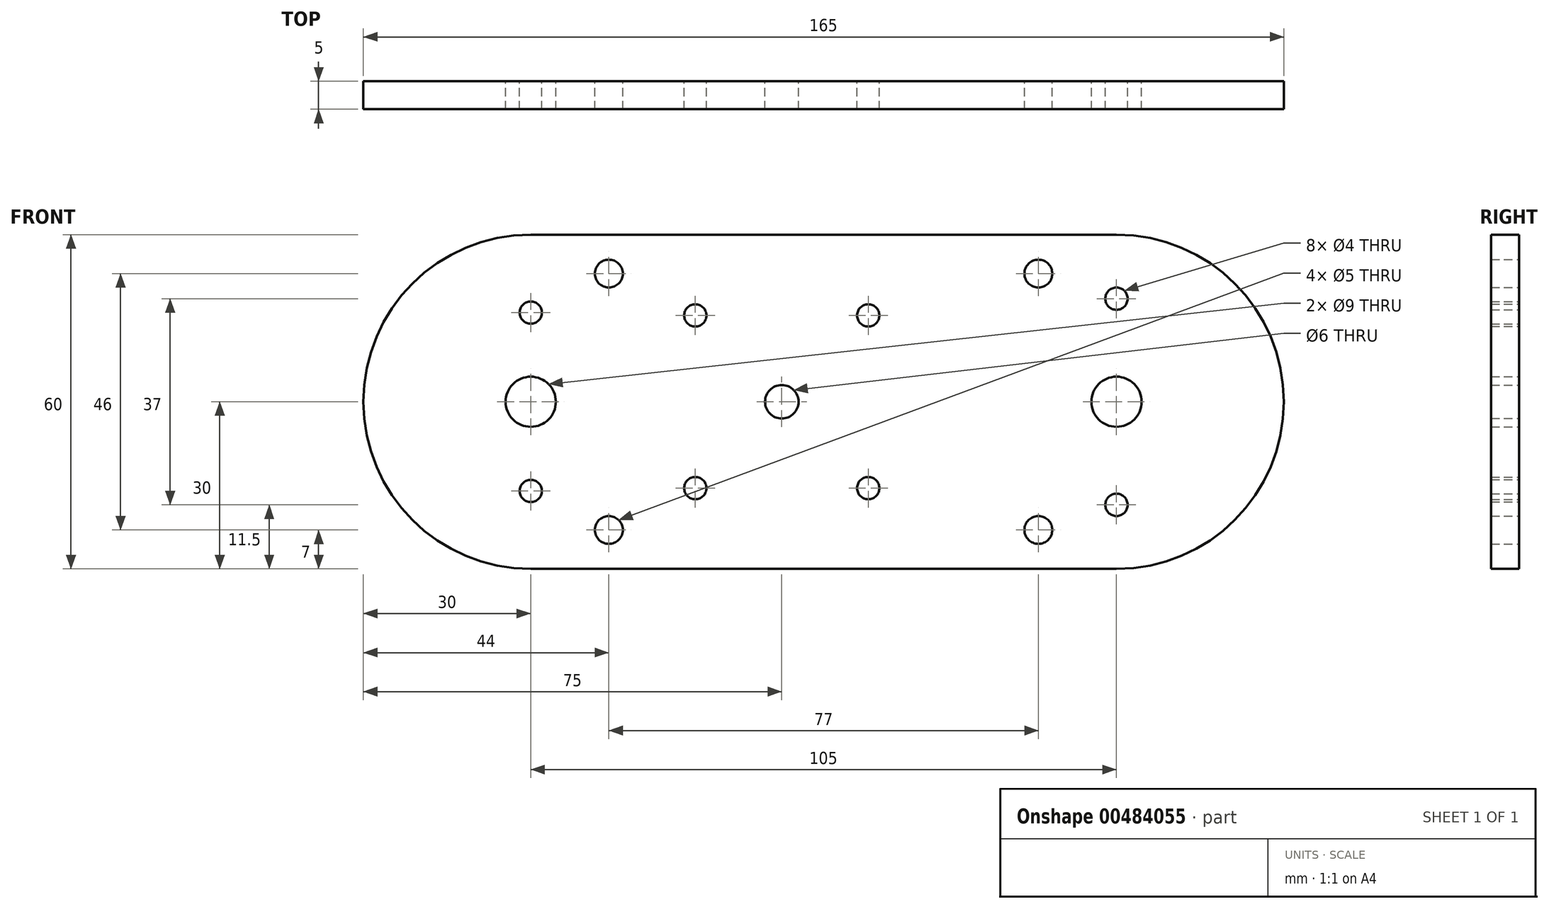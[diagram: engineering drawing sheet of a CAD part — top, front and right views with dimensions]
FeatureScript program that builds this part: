
annotation { "Feature Type Name" : "Feature", "Feature Type Description" : "" }
export const myFeature = defineFeature(function(context is Context, id is Id, definition is map)
    precondition{}
    {
        {
            var Q0;
            Q0=qCreatedBy(makeId("Front.planeOp"),FACE);
            var sketch = newSketch(context, id + "F0", { "sketchPlane" : qUnion([Q0])});
            skLineSegment(sketch, "E0.bottom", {"start": v(52.5, 30) * mm, "end": v(-52.5, 30) * mm});
            skLineSegment(sketch, "E0.top", {"start": v(52.5, -30) * mm, "end": v(-52.5, -30) * mm});
            skPoint(sketch, "E0.middle", {"position": v(0, 0) * mm});
            skArc(sketch, "E1", {"start": v(-52.5, 30) * mm, "mid": v(-82.5, 0) * mm, "end": v(-52.5, -30) * mm});
            skArc(sketch, "E2", {"start": v(52.5, 30) * mm, "mid": v(82.5, 0) * mm, "end": v(52.5, -30) * mm});
            skCircle(sketch, "E3", {"center": v(-52.5, 0) * mm, "radius": 4.5 * mm});
            skCircle(sketch, "E4", {"center": v(52.5, 0) * mm, "radius": 4.5 * mm});
            skPoint(sketch, "E5.middle", {"position": v(-7.5, 0) * mm});
            skCircle(sketch, "E6", {"center": v(-23, 15.5) * mm, "radius": 2 * mm});
            skCircle(sketch, "E7", {"center": v(8, 15.5) * mm, "radius": 2 * mm});
            skCircle(sketch, "E8", {"center": v(8, -15.5) * mm, "radius": 2 * mm});
            skCircle(sketch, "E9", {"center": v(-23, -15.5) * mm, "radius": 2 * mm});
            skCircle(sketch, "E10", {"center": v(-52.5, 16) * mm, "radius": 2 * mm});
            skCircle(sketch, "E11", {"center": v(-52.5, -16) * mm, "radius": 2 * mm});
            skCircle(sketch, "E12", {"center": v(52.5, 18.5) * mm, "radius": 2 * mm});
            skCircle(sketch, "E13", {"center": v(52.5, -18.5) * mm, "radius": 2 * mm});
            skCircle(sketch, "E14", {"center": v(-38.5, 23) * mm, "radius": 2.5 * mm});
            skCircle(sketch, "E15", {"center": v(-38.5, -23) * mm, "radius": 2.5 * mm});
            skCircle(sketch, "E16", {"center": v(38.5, -23) * mm, "radius": 2.5 * mm});
            skCircle(sketch, "E17", {"center": v(38.5, 23) * mm, "radius": 2.5 * mm});
            skCircle(sketch, "E18", {"center": v(-7.5, 0) * mm, "radius": 3 * mm});
            skSolve(sketch);
        }
        {
            var Q0;
            Q0 = qSketchRegion(id + "F0", true);
            extrude(context, id + "F1", {"entities" : qUnion([Q0]), "depth" : 5 * mm});
        }
    });
